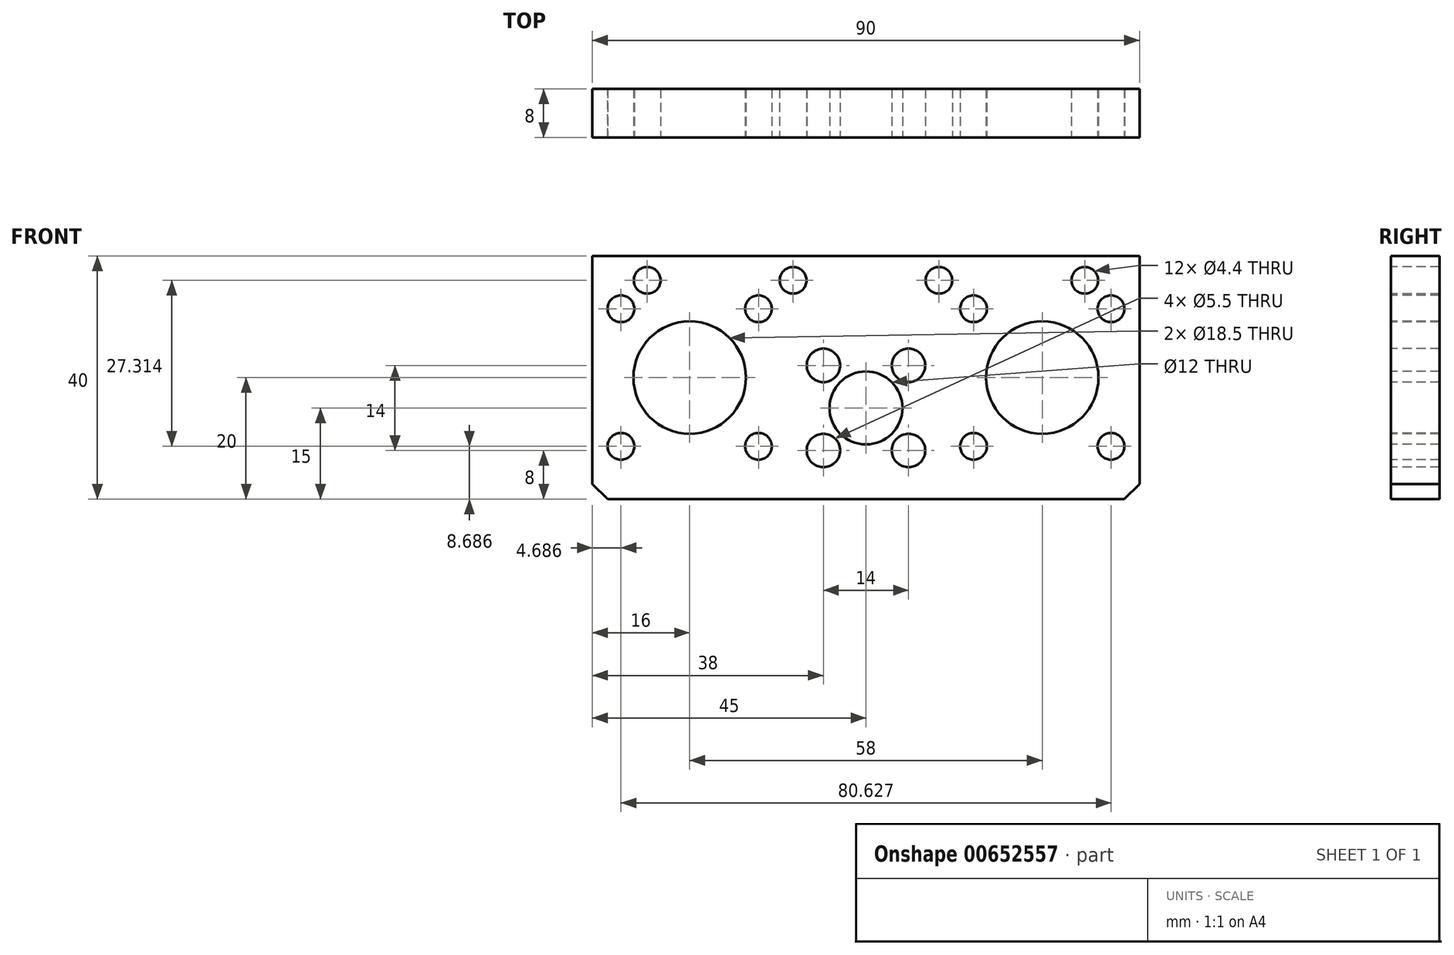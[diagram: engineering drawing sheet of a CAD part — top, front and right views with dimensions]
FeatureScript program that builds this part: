
annotation { "Feature Type Name" : "Feature", "Feature Type Description" : "" }
export const myFeature = defineFeature(function(context is Context, id is Id, definition is map)
    precondition{}
    {
        {
            var Q0;
            Q0=qCreatedBy(makeId("Front.planeOp"),FACE);
            var sketch = newSketch(context, id + "F0", { "sketchPlane" : qUnion([Q0])});
            skLineSegment(sketch, "E0.bottom", {"start": v(45, 20) * mm, "end": v(-45, 20) * mm});
            skLineSegment(sketch, "E0.top", {"start": v(45, -20) * mm, "end": v(-45, -20) * mm});
            skLineSegment(sketch, "E0.left", {"start": v(45, 20) * mm, "end": v(45, -20) * mm});
            skLineSegment(sketch, "E0.right", {"start": v(-45, 20) * mm, "end": v(-45, -20) * mm});
            skPoint(sketch, "E0.middle", {"position": v(0, 0) * mm});
            skSolve(sketch);
        }
        {
            var Q0;
            Q0 = qSketchRegion(id + "F0", true);
            extrude(context, id + "F1", {"entities" : qUnion([Q0]), "depth" : 8 * mm, "offsetDistance" : 25 * mm});
        }
        {
            var Q0;
            Q0=makeQuery(id+"F1.opExtrude","SWEPT_EDGE",EDGE,{"disambiguationData":[OSD([sQuery(id+"F0.wireOp",EDGE,"E0.top"),sQuery(id+"F0.wireOp",EDGE,"E0.right")])]});
            var Q1;
            Q1=makeQuery(id+"F1.opExtrude","SWEPT_EDGE",EDGE,{"disambiguationData":[OSD([sQuery(id+"F0.wireOp",EDGE,"E0.top"),sQuery(id+"F0.wireOp",EDGE,"E0.left")])]});
            chamfer(context, id + "F2", {"entities" : qUnion([Q0, Q1]), "width" : 2.5 * mm, "tangentPropagation" : true});
        }
        {
            var Q0;
            Q0=makeQuery(id+"F1.opExtrude","CAP_FACE",FACE,{"disambiguationData":[OSD([sQuery(id+"F0.wireOp",EDGE,"E0.bottom"),sQuery(id+"F0.wireOp",EDGE,"E0.top"),sQuery(id+"F0.wireOp",EDGE,"E0.left"),sQuery(id+"F0.wireOp",EDGE,"E0.right")])],"isStart":false});
            var sketch = newSketch(context, id + "F3", { "sketchPlane" : qUnion([Q0])});
            skPoint(sketch, "E1", {"position": v(0, -5) * mm});
            skPoint(sketch, "E2", {"position": v(29, 0) * mm});
            skPoint(sketch, "E3", {"position": v(-29, 0) * mm});
            skPoint(sketch, "E4", {"position": v(-7, 2) * mm});
            skPoint(sketch, "E5", {"position": v(7, 2) * mm});
            skPoint(sketch, "E6", {"position": v(7, -12) * mm});
            skPoint(sketch, "E7", {"position": v(-7, -12) * mm});
            skPoint(sketch, "E8", {"position": v(-40.31, -11.31) * mm});
            skPoint(sketch, "E9", {"position": v(-17.69, -11.31) * mm});
            skPoint(sketch, "E10", {"position": v(-17.69, 11.31) * mm});
            skPoint(sketch, "E11", {"position": v(-40.31, 11.31) * mm});
            skPoint(sketch, "E12", {"position": v(17.69, -11.31) * mm});
            skPoint(sketch, "E13", {"position": v(40.31, -11.31) * mm});
            skPoint(sketch, "E14", {"position": v(40.31, 11.31) * mm});
            skPoint(sketch, "E15", {"position": v(17.69, 11.31) * mm});
            skPoint(sketch, "E16", {"position": v(-36, 16) * mm});
            skPoint(sketch, "E17", {"position": v(-12, 16) * mm});
            skPoint(sketch, "E18", {"position": v(12, 16) * mm});
            skPoint(sketch, "E19", {"position": v(36, 16) * mm});
            skLineSegment(sketch, "E20", {"start": v(17.69, -11.31) * mm, "end": v(29, 0) * mm, "construction": true});
            skLineSegment(sketch, "E21", {"start": v(29, 0) * mm, "end": v(40.31, 11.31) * mm, "construction": true});
            skLineSegment(sketch, "E22", {"start": v(29, 0) * mm, "end": v(40.31, -11.31) * mm, "construction": true});
            skLineSegment(sketch, "E23", {"start": v(29, 0) * mm, "end": v(17.69, 11.31) * mm, "construction": true});
            skLineSegment(sketch, "E24", {"start": v(-29, 0) * mm, "end": v(-40.31, -11.31) * mm, "construction": true});
            skLineSegment(sketch, "E25", {"start": v(-17.69, -11.31) * mm, "end": v(-29, 0) * mm, "construction": true});
            skLineSegment(sketch, "E26", {"start": v(-29, 0) * mm, "end": v(-40.31, 11.31) * mm, "construction": true});
            skLineSegment(sketch, "E27", {"start": v(-29, 0) * mm, "end": v(-17.69, 11.31) * mm, "construction": true});
            skSolve(sketch);
        }
        {
            var Q0;
            Q0=sQuery(id+"F3.wireOp",VERTEX,"E16");
            var Q1;
            Q1=sQuery(id+"F3.wireOp",VERTEX,"E17");
            var Q2;
            Q2=sQuery(id+"F3.wireOp",VERTEX,"E18");
            var Q3;
            Q3=sQuery(id+"F3.wireOp",VERTEX,"E19");
            var Q4;
            Q4=makeQuery(id+"F1.opExtrude","SWEPT_BODY",BODY,{"disambiguationData":[OSD([sQuery(id+"F0.wireOp",EDGE,"E0.bottom"),sQuery(id+"F0.wireOp",EDGE,"E0.top"),sQuery(id+"F0.wireOp",EDGE,"E0.left"),sQuery(id+"F0.wireOp",EDGE,"E0.right")])]});
            hole(context, id + "F4", {"style" : HoleStyle.SIMPLE, "endStyle" : HoleEndStyle.THROUGH, "standardTappedOrClearance" : lookupTablePath({ "standard" : "ISO", "fit" : "Normal", "size" : "M4", "type" : "Clearance" }), "standardBlindInLast" : lookupTablePath({ "fit" : "Standard", "standard" : "ISO", "size" : "M4", "type" : "Clearance" }), "holeDiameter" : 4.4 * mm, "majorDiameter" : 4 * mm, "isTappedThrough" : true, "tappedDepth" : 12 * mm, "tapClearance" : 3, "locations" : qUnion([Q0, Q1, Q2, Q3]), "scope" : qUnion([Q4])});
        }
        {
            var Q0;
            Q0=sQuery(id+"F3.wireOp",VERTEX,"E11");
            var Q1;
            Q1=sQuery(id+"F3.wireOp",VERTEX,"E10");
            var Q2;
            Q2=sQuery(id+"F3.wireOp",VERTEX,"E9");
            var Q3;
            Q3=sQuery(id+"F3.wireOp",VERTEX,"E8");
            var Q4;
            Q4=sQuery(id+"F3.wireOp",VERTEX,"E15");
            var Q5;
            Q5=sQuery(id+"F3.wireOp",VERTEX,"E14");
            var Q6;
            Q6=sQuery(id+"F3.wireOp",VERTEX,"E13");
            var Q7;
            Q7=sQuery(id+"F3.wireOp",VERTEX,"E12");
            var Q8;
            Q8=makeQuery(id+"F1.opExtrude","SWEPT_BODY",BODY,{"disambiguationData":[OSD([sQuery(id+"F0.wireOp",EDGE,"E0.bottom"),sQuery(id+"F0.wireOp",EDGE,"E0.top"),sQuery(id+"F0.wireOp",EDGE,"E0.left"),sQuery(id+"F0.wireOp",EDGE,"E0.right")])]});
            hole(context, id + "F5", {"style" : HoleStyle.SIMPLE, "endStyle" : HoleEndStyle.THROUGH, "standardTappedOrClearance" : lookupTablePath({ "standard" : "ISO", "fit" : "Normal", "size" : "M4", "type" : "Clearance" }), "standardBlindInLast" : lookupTablePath({ "fit" : "Standard", "standard" : "ISO", "size" : "M4", "type" : "Clearance" }), "holeDiameter" : 4.4 * mm, "majorDiameter" : 5 * mm, "isTappedThrough" : true, "tappedDepth" : 12 * mm, "tapClearance" : 3, "locations" : qUnion([Q0, Q1, Q2, Q3, Q4, Q5, Q6, Q7]), "scope" : qUnion([Q8])});
        }
        {
            var Q0;
            Q0=sQuery(id+"F3.wireOp",VERTEX,"E3");
            var Q1;
            Q1=sQuery(id+"F3.wireOp",VERTEX,"E2");
            var Q2;
            Q2=makeQuery(id+"F1.opExtrude","SWEPT_BODY",BODY,{"disambiguationData":[OSD([sQuery(id+"F0.wireOp",EDGE,"E0.bottom"),sQuery(id+"F0.wireOp",EDGE,"E0.top"),sQuery(id+"F0.wireOp",EDGE,"E0.left"),sQuery(id+"F0.wireOp",EDGE,"E0.right")])]});
            hole(context, id + "F6", {"style" : HoleStyle.SIMPLE, "endStyle" : HoleEndStyle.THROUGH, "holeDiameter" : 18.5 * mm, "majorDiameter" : 5 * mm, "isTappedThrough" : true, "tappedDepth" : 12 * mm, "tapClearance" : 3, "locations" : qUnion([Q0, Q1]), "scope" : qUnion([Q2])});
        }
        {
            var Q0;
            Q0=sQuery(id+"F3.wireOp",VERTEX,"E1");
            var Q1;
            Q1=makeQuery(id+"F1.opExtrude","SWEPT_BODY",BODY,{"disambiguationData":[OSD([sQuery(id+"F0.wireOp",EDGE,"E0.bottom"),sQuery(id+"F0.wireOp",EDGE,"E0.top"),sQuery(id+"F0.wireOp",EDGE,"E0.left"),sQuery(id+"F0.wireOp",EDGE,"E0.right")])]});
            hole(context, id + "F7", {"style" : HoleStyle.SIMPLE, "endStyle" : HoleEndStyle.THROUGH, "holeDiameter" : 12 * mm, "majorDiameter" : 5 * mm, "isTappedThrough" : true, "tappedDepth" : 12 * mm, "tapClearance" : 3, "locations" : qUnion([Q0]), "scope" : qUnion([Q1])});
        }
        {
            var Q0;
            Q0=sQuery(id+"F3.wireOp",VERTEX,"E6");
            var Q1;
            Q1=sQuery(id+"F3.wireOp",VERTEX,"E4");
            var Q2;
            Q2=sQuery(id+"F3.wireOp",VERTEX,"E5");
            var Q3;
            Q3=sQuery(id+"F3.wireOp",VERTEX,"E7");
            var Q4;
            Q4=makeQuery(id+"F1.opExtrude","SWEPT_BODY",BODY,{"disambiguationData":[OSD([sQuery(id+"F0.wireOp",EDGE,"E0.bottom"),sQuery(id+"F0.wireOp",EDGE,"E0.top"),sQuery(id+"F0.wireOp",EDGE,"E0.left"),sQuery(id+"F0.wireOp",EDGE,"E0.right")])]});
            hole(context, id + "F8", {"style" : HoleStyle.SIMPLE, "endStyle" : HoleEndStyle.THROUGH, "holeDiameter" : 5.5 * mm, "majorDiameter" : 5 * mm, "isTappedThrough" : true, "tappedDepth" : 12 * mm, "tapClearance" : 3, "locations" : qUnion([Q0, Q1, Q2, Q3]), "scope" : qUnion([Q4])});
        }
    });
